# Revit family: Dyyni
name_source: partatom
category: Furniture
revit_build: Autodesk Revit 2015 (Build: 20140606_1530(x64)
units: mm (PartAtom-declared; Revit-internal decimal feet)

## types (12) — shared parameters
Manufacturer = Isku Oy
Seat 1 invisibility = Yes
Type Comments = Available as antimicrobial
URL = www.isku.fi

## per-type parameters (varying)
| type | Armrest left | Armrest right | Back support 1 visibility | Back support 2 visibility | Back support 3 visibility | Frame Material | Middle leg visibility | Seat 2 invisibility | Seat 3 invisibility | Width |
| Dyyni 3732 Sofa 3-persons, width 1800 - with armsrest and back support | Yes | Yes | Yes | Yes | Yes | <By Category> | Yes | Yes | Yes | 1719 mm |
| Dyyni 3732 chair, width 600 - with armrest and back support | Yes | Yes | Yes | No | No | <By Category> | No | No | No | 518 mm  [stored 1.69948 ft] |
| Dyyni 3732 Sofa 2-persons, width 1200 - with armsrest and back support | Yes | Yes | Yes | Yes | No | <By Category> | No | Yes | No | 1118 mm |
| Dyyni 3732 Sofa 3-persons, width 1800 - no armsrest no back support | No | No | No | No | No | <By Category> | Yes | Yes | Yes | 1719 mm |
| Dyyni 3732 Sofa 2-persons, width 1200 - no armsrest no back support | No | No | No | No | No | <By Category> | No | Yes | No | 1118 mm |
| Dyyni 3732 Sofa 3-persons, width 1800 - with left armsrest and back support | Yes | No | Yes | Yes | Yes | <By Category> | Yes | Yes | Yes | 1719 mm |
| Dyyni 3732 Sofa 2-persons, width 1200 - with left armsrest and back support | Yes | No | Yes | Yes | No | <By Category> | No | Yes | No | 1118 mm |
| Dyyni 3732 chair, width 600 - right armrest and back support | No | Yes | Yes | No | No | Steel, chrome | No | No | No | 518 mm  [stored 1.69948 ft] |
| Dyyni 3732 chair, width 600 - no armrest no back support | No | No | No | No | No | <By Category> | No | No | No | 518 mm  [stored 1.69948 ft] |
| Dyyni 3732 Sofa 2-persons, width 1200 - with right armsrest and back support | No | Yes | Yes | Yes | No | <By Category> | No | Yes | No | 1118 mm |
| Dyyni 3732 Sofa 3-persons, width 1800 - with right armsrest and back support | No | Yes | Yes | Yes | Yes | <By Category> | Yes | Yes | Yes | 1719 mm |
| Dyyni 3732 chair, width 600 - left armrest and back support | Yes | No | Yes | No | No | Steel, chrome | No | No | No | 518 mm  [stored 1.69948 ft] |

note: [stored X ft] marks values corroborated as IEEE doubles in the binary element streams (Revit-internal decimal feet)

## geometry (parser evidence)
native form markers: Sweep x19
no freeform markers — native parametric forms only
